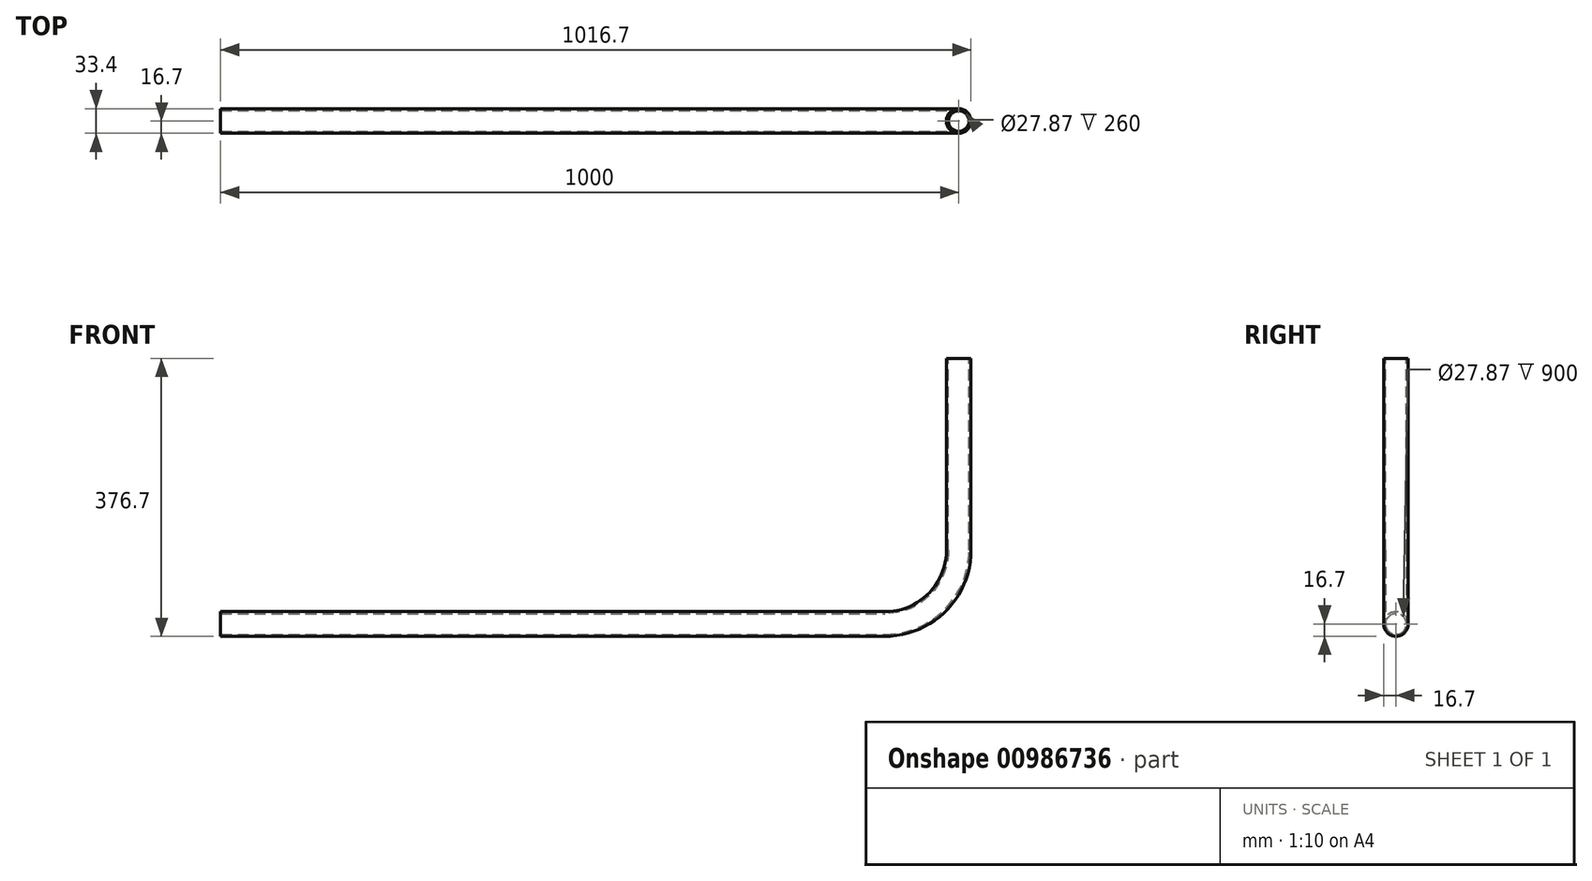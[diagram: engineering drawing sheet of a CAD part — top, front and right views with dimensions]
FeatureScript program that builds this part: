
annotation { "Feature Type Name" : "Feature", "Feature Type Description" : "" }
export const myFeature = defineFeature(function(context is Context, id is Id, definition is map)
    precondition{}
    {
        {
            var Q0;
            Q0=qCreatedBy(makeId("Front.planeOp"),FACE);
            var sketch = newSketch(context, id + "F0", { "sketchPlane" : qUnion([Q0])});
            skLineSegment(sketch, "E0", {"start": v(0, 0) * mm, "end": v(900, 0) * mm});
            skLineSegment(sketch, "E1", {"start": v(1000, 100) * mm, "end": v(1000, 360) * mm});
            skPoint(sketch, "E2.visualSharp", {"position": v(1000, 0) * mm});
            skArc(sketch, "E2.filletArc", {"start": v(900, 0) * mm, "mid": v(970.71, 29.29) * mm, "end": v(1000, 100) * mm});
            skSolve(sketch);
        }
        {
            var Q0;
            Q0=qCreatedBy(makeId("Right.planeOp"),FACE);
            var sketch = newSketch(context, id + "F1", { "sketchPlane" : qUnion([Q0])});
            skCircle(sketch, "E3", {"center": v(0, 0) * mm, "radius": 16.7 * mm});
            skCircle(sketch, "E4.0", {"center": v(0, 0) * mm, "radius": 13.93 * mm});
            skSolve(sketch);
        }
        {
            var Q0;
            Q0=makeQuery(id+"F1.imprint","IMPRINT",FACE,{"disambiguationData":[TD([[makeQuery(id+"F1.imprint","IMPRINT",EDGE,{"derivedFrom":sQuery(id+"F1.wireOp",EDGE,"E3")}),1.0]])]});
            var Q1;
            Q1=sQuery(id+"F0.wireOp",EDGE,"E0");
            var Q2;
            Q2=sQuery(id+"F0.wireOp",EDGE,"E2.filletArc");
            var Q3;
            Q3=sQuery(id+"F0.wireOp",EDGE,"E1");
            sweep(context, id + "F2", {"profiles" : qUnion([Q0]), "path" : qUnion([Q1, Q2, Q3])});
        }
    });
